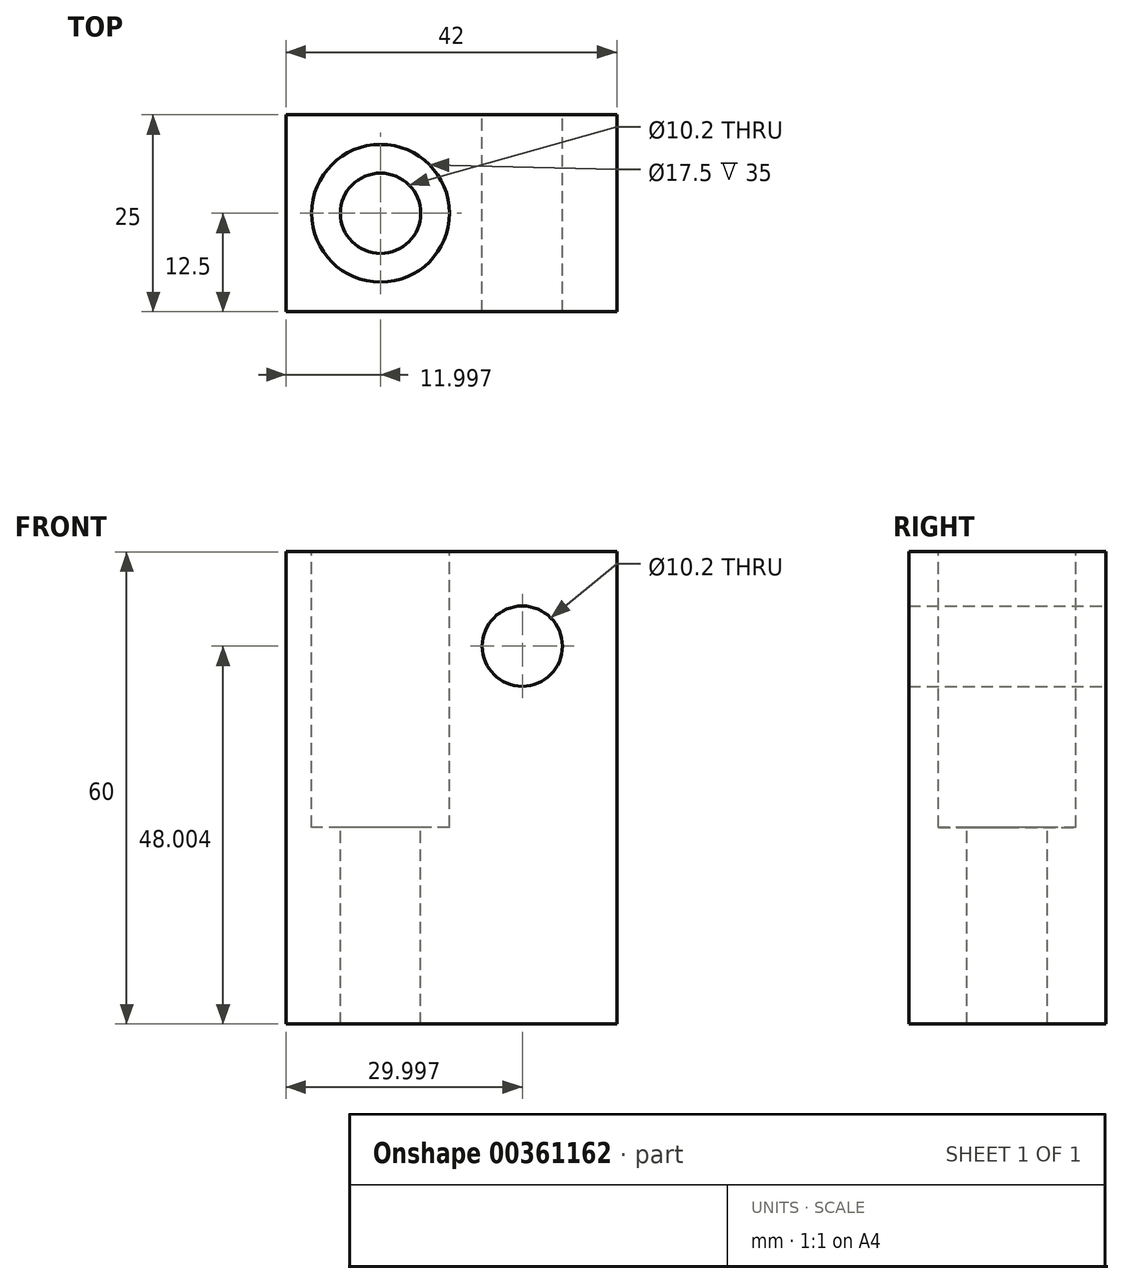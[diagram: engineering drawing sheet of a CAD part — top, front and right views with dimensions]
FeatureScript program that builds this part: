
annotation { "Feature Type Name" : "Feature", "Feature Type Description" : "" }
export const myFeature = defineFeature(function(context is Context, id is Id, definition is map)
    precondition{}
    {
        {
            var Q0;
            Q0=qCreatedBy(makeId("Front.planeOp"),FACE);
            var sketch = newSketch(context, id + "F0", { "sketchPlane" : qUnion([Q0])});
            skLineSegment(sketch, "E0", {"start": v(-95.8, -46.03) * mm, "end": v(-95.8, 13.97) * mm});
            skLineSegment(sketch, "E1", {"start": v(-95.8, 13.97) * mm, "end": v(-53.8, 13.97) * mm});
            skLineSegment(sketch, "E2", {"start": v(-53.8, 13.97) * mm, "end": v(-53.8, -46.03) * mm});
            skLineSegment(sketch, "E3", {"start": v(-53.8, -46.03) * mm, "end": v(-95.8, -46.03) * mm});
            skLineSegment(sketch, "E4.bottom", {"start": v(-53.8, 13.97) * mm, "end": v(-65.8, 13.97) * mm});
            skLineSegment(sketch, "E4.left", {"start": v(-53.8, 13.97) * mm, "end": v(-53.8, 1.97) * mm});
            skCircle(sketch, "E5", {"center": v(-65.8, 1.97) * mm, "radius": 5.1 * mm});
            skSolve(sketch);
        }
        {
            var Q0;
            Q0=makeQuery(id+"F0.imprint","IMPRINT",FACE,{"disambiguationData":[TD([[makeQuery(id+"F0.imprint","IMPRINT",EDGE,{"derivedFrom":sQuery(id+"F0.wireOp",EDGE,"E0")}),-1.0]])]});
            extrude(context, id + "F1", {"entities" : qUnion([Q0]), "depth" : 25 * mm});
        }
        {
            var Q0;
            Q0=makeQuery(id+"F1.opExtrude","SWEPT_FACE",FACE,{"disambiguationData":[OSD([sQuery(id+"F0.wireOp",EDGE,"E1"),sQuery(id+"F0.wireOp",EDGE,"E4.bottom")])]});
            var sketch = newSketch(context, id + "F2", { "sketchPlane" : qUnion([Q0])});
            skCircle(sketch, "E6", {"center": v(-83.8, -12.5) * mm, "radius": 5.1 * mm});
            skCircle(sketch, "E7", {"center": v(-83.8, -12.5) * mm, "radius": 8.75 * mm});
            skSolve(sketch);
        }
        {
            var Q0;
            Q0=makeQuery(id+"F2.imprint","IMPRINT",FACE,{"disambiguationData":[TD([[makeQuery(id+"F2.imprint","IMPRINT",EDGE,{"derivedFrom":sQuery(id+"F2.wireOp",EDGE,"E6")}),1.0]])]});
            extrude(context, id + "F3", {"entities" : qUnion([Q0]), "operationType" : NewBodyOperationType.REMOVE, "oppositeDirection" : true, "depth" : 63.5 * mm});
        }
        {
            var Q0;
            Q0=makeQuery(id+"F2.imprint","IMPRINT",FACE,{"disambiguationData":[TD([[makeQuery(id+"F2.imprint","IMPRINT",EDGE,{"derivedFrom":sQuery(id+"F2.wireOp",EDGE,"E6")}),-1.0]])]});
            extrude(context, id + "F4", {"entities" : qUnion([Q0]), "operationType" : NewBodyOperationType.REMOVE, "oppositeDirection" : true, "depth" : 35 * mm});
        }
    });
